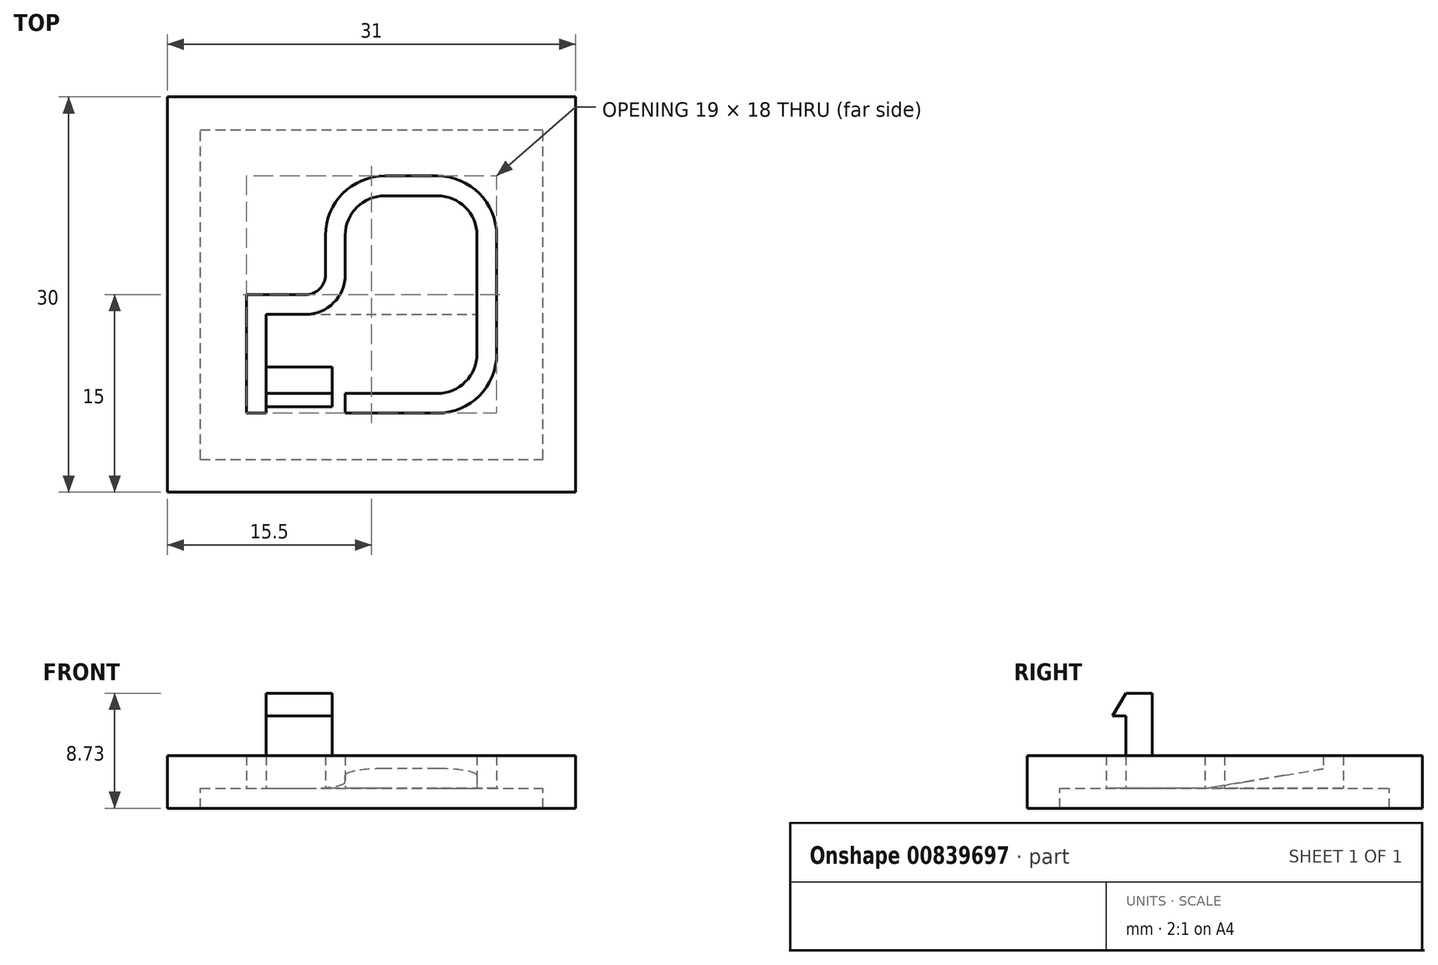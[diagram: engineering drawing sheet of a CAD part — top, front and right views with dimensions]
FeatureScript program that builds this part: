
annotation { "Feature Type Name" : "Feature", "Feature Type Description" : "" }
export const myFeature = defineFeature(function(context is Context, id is Id, definition is map)
    precondition{}
    {
        {
            var Q0;
            Q0=qCreatedBy(makeId("Top.planeOp"),FACE);
            var sketch = newSketch(context, id + "F0", { "sketchPlane" : qUnion([Q0])});
            skLineSegment(sketch, "E0.bottom", {"start": v(0, 0) * mm, "end": v(31, 0) * mm});
            skLineSegment(sketch, "E0.top", {"start": v(0, 30) * mm, "end": v(31, 30) * mm});
            skLineSegment(sketch, "E0.left", {"start": v(0, 0) * mm, "end": v(0, 30) * mm});
            skLineSegment(sketch, "E0.right", {"start": v(31, 0) * mm, "end": v(31, 30) * mm});
            skLineSegment(sketch, "E1.bottom", {"start": v(7.5, 13.5) * mm, "end": v(10.5, 13.5) * mm});
            skLineSegment(sketch, "E1.top", {"start": v(7.5, 7.5) * mm, "end": v(13.5, 7.5) * mm, "construction": true});
            skLineSegment(sketch, "E1.left", {"start": v(7.5, 13.5) * mm, "end": v(7.5, 7.5) * mm});
            skLineSegment(sketch, "E2.bottom", {"start": v(20.5, 22.5) * mm, "end": v(16.5, 22.5) * mm});
            skLineSegment(sketch, "E2.top", {"start": v(20.5, 7.5) * mm, "end": v(13.5, 7.5) * mm});
            skLineSegment(sketch, "E2.left", {"start": v(23.5, 19.5) * mm, "end": v(23.5, 10.5) * mm});
            skLineSegment(sketch, "E3", {"start": v(13.5, 7.5) * mm, "end": v(13.5, 13.5) * mm, "construction": true});
            skLineSegment(sketch, "E4", {"start": v(13.5, 16.5) * mm, "end": v(13.5, 19.5) * mm});
            skPoint(sketch, "E5.visualSharp", {"position": v(13.5, 22.5) * mm});
            skArc(sketch, "E5.filletArc", {"start": v(16.5, 22.5) * mm, "mid": v(14.38, 21.62) * mm, "end": v(13.5, 19.5) * mm});
            skPoint(sketch, "E6.visualSharp", {"position": v(23.5, 22.5) * mm});
            skArc(sketch, "E6.filletArc", {"start": v(23.5, 19.5) * mm, "mid": v(22.62, 21.62) * mm, "end": v(20.5, 22.5) * mm});
            skPoint(sketch, "E7.visualSharp", {"position": v(23.5, 7.5) * mm});
            skArc(sketch, "E7.filletArc", {"start": v(20.5, 7.5) * mm, "mid": v(22.62, 8.38) * mm, "end": v(23.5, 10.5) * mm});
            skPoint(sketch, "E8.visualSharp", {"position": v(13.5, 13.5) * mm});
            skArc(sketch, "E8.filletArc", {"start": v(10.5, 13.5) * mm, "mid": v(12.62, 14.38) * mm, "end": v(13.5, 16.5) * mm});
            skLineSegment(sketch, "E9.0", {"start": v(20.5, 6) * mm, "end": v(13.5, 6) * mm});
            skArc(sketch, "E9.1", {"start": v(20.5, 6) * mm, "mid": v(23.68, 7.32) * mm, "end": v(25, 10.5) * mm});
            skLineSegment(sketch, "E9.2", {"start": v(25, 19.5) * mm, "end": v(25, 10.5) * mm});
            skArc(sketch, "E9.3", {"start": v(25, 19.5) * mm, "mid": v(23.68, 22.68) * mm, "end": v(20.5, 24) * mm});
            skLineSegment(sketch, "E9.4", {"start": v(20.5, 24) * mm, "end": v(16.5, 24) * mm});
            skArc(sketch, "E9.5", {"start": v(16.5, 24) * mm, "mid": v(13.32, 22.68) * mm, "end": v(12, 19.5) * mm});
            skLineSegment(sketch, "E9.6", {"start": v(6, 15) * mm, "end": v(6, 6) * mm});
            skLineSegment(sketch, "E9.7", {"start": v(6, 15) * mm, "end": v(10.5, 15) * mm});
            skArc(sketch, "E9.8", {"start": v(10.5, 15) * mm, "mid": v(11.56, 15.44) * mm, "end": v(12, 16.5) * mm});
            skLineSegment(sketch, "E9.9", {"start": v(12, 16.5) * mm, "end": v(12, 19.5) * mm});
            skLineSegment(sketch, "E10", {"start": v(13.5, 7.5) * mm, "end": v(13.5, 6) * mm});
            skLineSegment(sketch, "E11", {"start": v(6, 6) * mm, "end": v(7.5, 6) * mm});
            skLineSegment(sketch, "E12", {"start": v(7.5, 6) * mm, "end": v(7.5, 7.5) * mm});
            skLineSegment(sketch, "E13", {"start": v(13.5, 6) * mm, "end": v(7.5, 6) * mm, "construction": true});
            skSolve(sketch);
        }
        {
            var Q0;
            Q0 = qSketchRegion(id + "F0", true);
            extrude(context, id + "F1", {"entities" : qUnion([Q0]), "depth" : 2.5 * mm, "offsetDistance" : 25 * mm});
        }
        {
            var Q0;
            Q0=makeQuery(id+"F1.opExtrude","CAP_FACE",FACE,{"disambiguationData":[OSD([sQuery(id+"F0.wireOp",EDGE,"E0.bottom"),sQuery(id+"F0.wireOp",EDGE,"E0.top"),sQuery(id+"F0.wireOp",EDGE,"E0.left"),sQuery(id+"F0.wireOp",EDGE,"E0.right"),sQuery(id+"F0.wireOp",EDGE,"E1.bottom"),sQuery(id+"F0.wireOp",EDGE,"E1.left"),sQuery(id+"F0.wireOp",EDGE,"E2.bottom"),sQuery(id+"F0.wireOp",EDGE,"E2.top"),sQuery(id+"F0.wireOp",EDGE,"E2.left"),sQuery(id+"F0.wireOp",EDGE,"E4"),sQuery(id+"F0.wireOp",EDGE,"E5.filletArc"),sQuery(id+"F0.wireOp",EDGE,"E6.filletArc"),sQuery(id+"F0.wireOp",EDGE,"E7.filletArc"),sQuery(id+"F0.wireOp",EDGE,"E8.filletArc"),sQuery(id+"F0.wireOp",EDGE,"E9.0"),sQuery(id+"F0.wireOp",EDGE,"E9.1"),sQuery(id+"F0.wireOp",EDGE,"E9.2"),sQuery(id+"F0.wireOp",EDGE,"E9.3"),sQuery(id+"F0.wireOp",EDGE,"E9.4"),sQuery(id+"F0.wireOp",EDGE,"E9.5"),sQuery(id+"F0.wireOp",EDGE,"E9.6"),sQuery(id+"F0.wireOp",EDGE,"E9.7"),sQuery(id+"F0.wireOp",EDGE,"E9.8"),sQuery(id+"F0.wireOp",EDGE,"E9.9"),sQuery(id+"F0.wireOp",EDGE,"E10"),sQuery(id+"F0.wireOp",EDGE,"E11"),sQuery(id+"F0.wireOp",EDGE,"E12")])],"isStart":true});
            var sketch = newSketch(context, id + "F2", { "sketchPlane" : qUnion([Q0])});
            skLineSegment(sketch, "E14.0", {"start": v(31, 0) * mm, "end": v(31, -30) * mm});
            skLineSegment(sketch, "E14.1", {"start": v(0, -30) * mm, "end": v(31, -30) * mm});
            skLineSegment(sketch, "E14.2", {"start": v(0, 0) * mm, "end": v(0, -30) * mm});
            skLineSegment(sketch, "E14.3", {"start": v(0, 0) * mm, "end": v(31, 0) * mm});
            skLineSegment(sketch, "E15.0", {"start": v(2.5, -2.5) * mm, "end": v(28.5, -2.5) * mm});
            skLineSegment(sketch, "E15.1", {"start": v(2.5, -2.5) * mm, "end": v(2.5, -27.5) * mm});
            skLineSegment(sketch, "E15.2", {"start": v(2.5, -27.5) * mm, "end": v(28.5, -27.5) * mm});
            skLineSegment(sketch, "E15.3", {"start": v(28.5, -2.5) * mm, "end": v(28.5, -27.5) * mm});
            skSolve(sketch);
        }
        {
            var Q0;
            Q0 = qSketchRegion(id + "F2", true);
            extrude(context, id + "F3", {"entities" : qUnion([Q0]), "operationType" : NewBodyOperationType.ADD, "depth" : 1.5 * mm, "offsetDistance" : 25 * mm});
        }
        {
            var Q0;
            Q0=makeQuery(id+"F1.opExtrude","SWEPT_FACE",FACE,{"disambiguationData":[OSD([sQuery(id+"F0.wireOp",EDGE,"E1.left"),sQuery(id+"F0.wireOp",EDGE,"E12")])]});
            var sketch = newSketch(context, id + "F4", { "sketchPlane" : qUnion([Q0])});
            skPoint(sketch, "E16.0", {"position": v(-7.5, 2.5) * mm});
            skLineSegment(sketch, "E17", {"start": v(-7.5, 2.5) * mm, "end": v(-7.5, 5.5) * mm});
            skLineSegment(sketch, "E18", {"start": v(-7.5, 5.5) * mm, "end": v(-6.5, 5.5) * mm});
            skLineSegment(sketch, "E19", {"start": v(-6.5, 5.5) * mm, "end": v(-7.5, 7.23) * mm});
            skLineSegment(sketch, "E20", {"start": v(-7.5, 7.23) * mm, "end": v(-9.5, 7.23) * mm});
            skLineSegment(sketch, "E21", {"start": v(-9.5, 7.23) * mm, "end": v(-9.5, 2.5) * mm});
            skLineSegment(sketch, "E22", {"start": v(-9.5, 2.5) * mm, "end": v(-7.5, 2.5) * mm});
            skSolve(sketch);
        }
        {
            var Q0;
            Q0 = qSketchRegion(id + "F4", true);
            var Q1;
            Q1=makeQuery(id+"F1.opExtrude","SWEPT_FACE",FACE,{"disambiguationData":[OSD([sQuery(id+"F0.wireOp",EDGE,"E10")])]});
            extrude(context, id + "F5", {"entities" : qUnion([Q0]), "operationType" : NewBodyOperationType.ADD, "endBound" : BoundingType.UP_TO_SURFACE, "oppositeDirection" : true, "depth" : 25 * mm, "endBoundEntityFace" : qUnion([Q1]), "hasOffset" : true, "offsetDistance" : 1 * mm});
        }
        {
            var Q0;
            Q0=makeQuery(id+"F1.opExtrude","CAP_EDGE",EDGE,{"disambiguationData":[OSD([sQuery(id+"F0.wireOp",EDGE,"E2.bottom")])],"isStart":true});
            chamfer(context, id + "F6", {"entities" : qUnion([Q0]), "chamferType" : ChamferType.TWO_OFFSETS, "width1" : 1.5 * mm, "oppositeDirection" : false, "width2" : 9 * mm});
        }
    });
